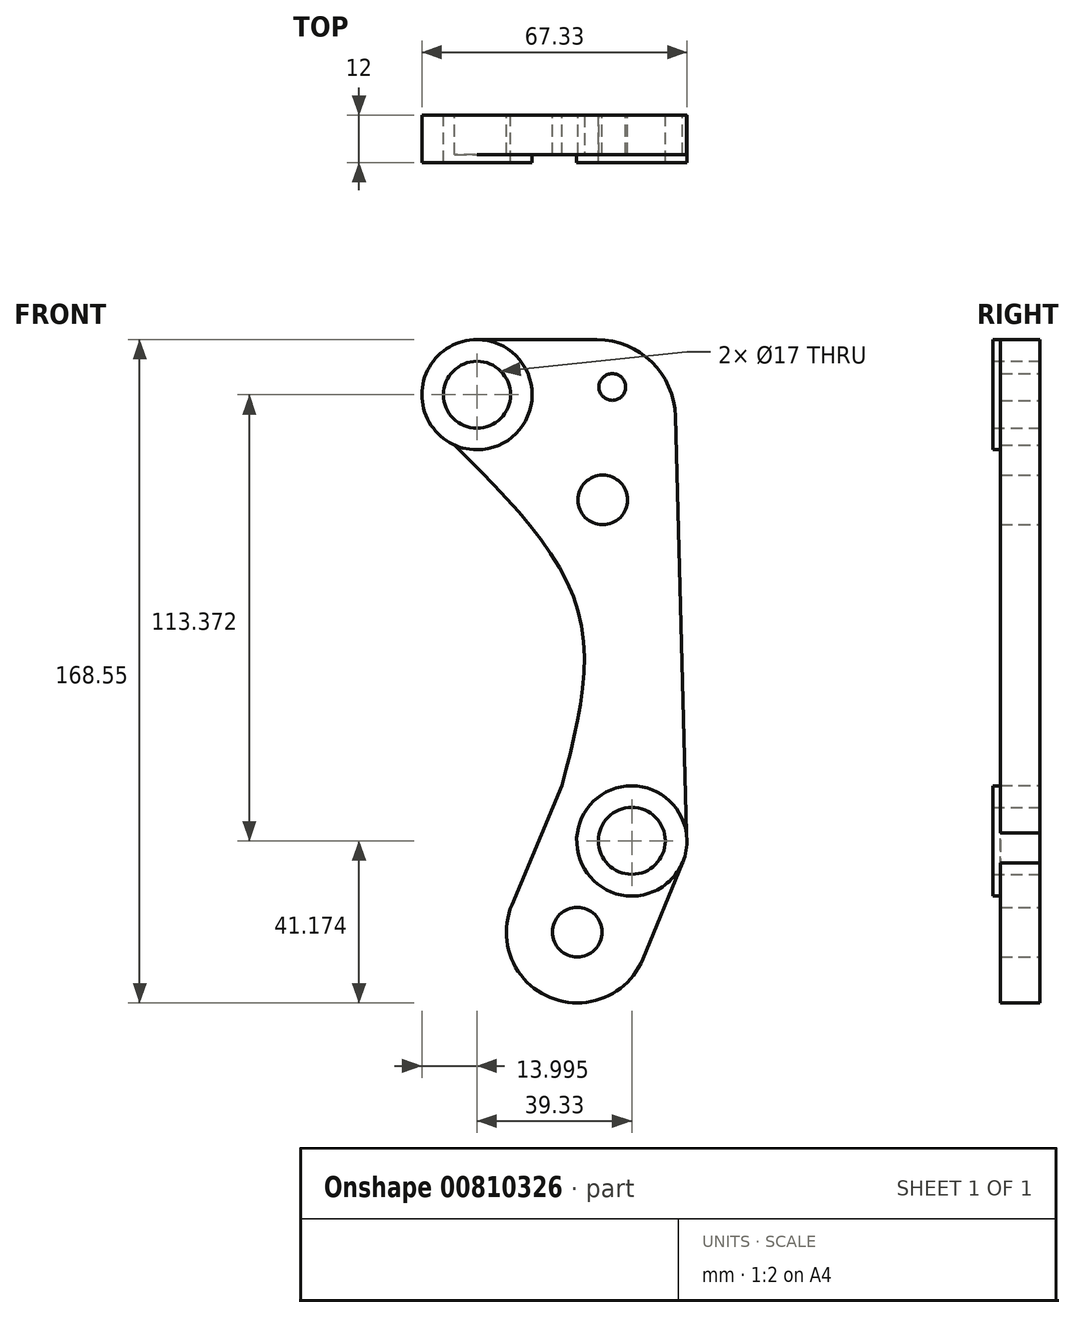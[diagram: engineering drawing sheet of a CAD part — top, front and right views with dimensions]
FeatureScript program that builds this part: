
annotation { "Feature Type Name" : "Feature", "Feature Type Description" : "" }
export const myFeature = defineFeature(function(context is Context, id is Id, definition is map)
    precondition{}
    {
        {
            var Q0;
            Q0=qCreatedBy(makeId("Front.planeOp"),FACE);
            var sketch = newSketch(context, id + "F0", { "sketchPlane" : qUnion([Q0])});
            skCircle(sketch, "E0", {"center": v(31.19, -37.2) * mm, "radius": 6.3 * mm});
            skCircle(sketch, "E1", {"center": v(37.66, 72.6) * mm, "radius": 6.3 * mm});
            skCircle(sketch, "E2", {"center": v(45.05, -14.04) * mm, "radius": 8.5 * mm});
            skCircle(sketch, "E3", {"center": v(45.05, -14.04) * mm, "radius": 14 * mm});
            skArc(sketch, "E4", {"start": v(14.6, -30.24) * mm, "mid": v(24.28, -53.83) * mm, "end": v(47.84, -44.06) * mm});
            skCircle(sketch, "E5", {"center": v(31.19, -37.2) * mm, "radius": 9 * mm});
            skCircle(sketch, "E6", {"center": v(37.66, 72.6) * mm, "radius": 9 * mm});
            skLineSegment(sketch, "E7", {"start": v(57.9, -19.57) * mm, "end": v(47.84, -44.06) * mm});
            skCircle(sketch, "E8", {"center": v(5.72, 99.34) * mm, "radius": 8.5 * mm});
            skCircle(sketch, "E9", {"center": v(5.72, 99.34) * mm, "radius": 14 * mm});
            skArc(sketch, "E10", {"start": v(56.14, 93.81) * mm, "mid": v(50.12, 107.61) * mm, "end": v(36.18, 113.3) * mm});
            skCircle(sketch, "E11", {"center": v(40.1, 101.3) * mm, "radius": 3.4 * mm});
            skLineSegment(sketch, "E12", {"start": v(36.18, 113.3) * mm, "end": v(5.73, 113.34) * mm});
            skLineSegment(sketch, "E13", {"start": v(58.9, -11.97) * mm, "end": v(56.14, 93.81) * mm});
            skLineSegment(sketch, "E14", {"start": v(14.6, -30.24) * mm, "end": v(27.3, 0) * mm});
            skFitSpline(sketch, "E15", {"points": [v(27.3, 0) * mm, v(31.38, 44.5) * mm, v(0, 86.56) * mm], "startDerivative": vector(25.04, 95.56) * mm, "endDerivative": vector(-78.25, 77.8) * mm});
            skSolve(sketch);
        }
        {
            var Q0;
            Q0=makeQuery(id+"F0.imprint","IMPRINT",FACE,{"disambiguationData":[TD([[makeQuery(id+"F0.imprint","IMPRINT",EDGE,{"derivedFrom":sQuery(id+"F0.wireOp",EDGE,"E2")}),-1.0]])]});
            var Q1;
            Q1=makeQuery(id+"F0.imprint","IMPRINT",FACE,{"disambiguationData":[TD([[makeQuery(id+"F0.imprint","IMPRINT",EDGE,{"derivedFrom":sQuery(id+"F0.wireOp",EDGE,"SP4YICm1-ePz9-ccjE-kNvD-3VjDllcA9a2P")}),1.0]])]});
            var Q2;
            Q2=makeQuery(id+"F0.imprint","IMPRINT",FACE,{"disambiguationData":[TD([[makeQuery(id+"F0.imprint","IMPRINT",EDGE,{"derivedFrom":sQuery(id+"F0.wireOp",EDGE,"E1")}),-1.0]])]});
            var Q3;
            {var subQ0=sQuery(id+"F0.wireOp",EDGE,"E7");Q3=makeQuery(id+"F0.imprint","IMPRINT",FACE,{"disambiguationData":[TD([[makeQuery(id+"F0.imprint","IMPRINT",EDGE,{"derivedFrom":subQ0}),-1.0]])]});}
            var Q4;
            Q4=makeQuery(id+"F0.imprint","IMPRINT",FACE,{"disambiguationData":[TD([[makeQuery(id+"F0.imprint","IMPRINT",EDGE,{"derivedFrom":sQuery(id+"F0.wireOp",EDGE,"E8")}),-1.0]])]});
            var Q5;
            Q5=makeQuery(id+"F0.imprint","IMPRINT",FACE,{"disambiguationData":[TD([[makeQuery(id+"F0.imprint","IMPRINT",EDGE,{"derivedFrom":sQuery(id+"F0.wireOp",EDGE,"E5")}),-1.0]])]});
            var Q6;
            {var subQ2=sQuery(id+"F0.wireOp",EDGE,"E3");var subQ4=sQuery(id+"F0.wireOp",EDGE,"EtesAAMI-uVo2-qHGR-uLT1-KKP0nME1nuCn");var subQ5=makeQuery(id+"F0.imprint","INTERSECT",VERTEX,{"disambiguationData":[OD(0.0)],"derivedFrom":[subQ4,subQ2]});Q6=makeQuery(id+"F0.imprint","IMPRINT",FACE,{"disambiguationData":[TD([[makeQuery(id+"F0.imprint","IMPRINT",EDGE,{"disambiguationData":[TD([[subQ5,-1.0]])],"derivedFrom":subQ4}),-1.0]])]});}
            var Q7;
            Q7=makeQuery(id+"F0.imprint","IMPRINT",FACE,{"disambiguationData":[TD([[makeQuery(id+"F0.imprint","IMPRINT",EDGE,{"derivedFrom":sQuery(id+"F0.wireOp",EDGE,"SP4YICm1-ePz9-ccjE-kNvD-3VjDllcA9a2P")}),-1.0]])]});
            var Q8;
            Q8=makeQuery(id+"F0.imprint","IMPRINT",FACE,{"disambiguationData":[TD([[makeQuery(id+"F0.imprint","IMPRINT",EDGE,{"derivedFrom":sQuery(id+"F0.wireOp",EDGE,"E0")}),1.0]])]});
            var Q9;
            Q9=makeQuery(id+"F0.imprint","IMPRINT",FACE,{"disambiguationData":[TD([[makeQuery(id+"F0.imprint","IMPRINT",EDGE,{"derivedFrom":sQuery(id+"F0.wireOp",EDGE,"E1")}),1.0]])]});
            var Q10;
            Q10=makeQuery(id+"F0.imprint","IMPRINT",FACE,{"disambiguationData":[TD([[makeQuery(id+"F0.imprint","IMPRINT",EDGE,{"derivedFrom":sQuery(id+"F0.wireOp",EDGE,"E2")}),1.0]])]});
            var Q11;
            Q11=makeQuery(id+"F0.imprint","IMPRINT",FACE,{"disambiguationData":[TD([[makeQuery(id+"F0.imprint","IMPRINT",EDGE,{"derivedFrom":sQuery(id+"F0.wireOp",EDGE,"E8")}),1.0]])]});
            var Q12;
            Q12=makeQuery(id+"F0.imprint","IMPRINT",FACE,{"disambiguationData":[TD([[makeQuery(id+"F0.imprint","IMPRINT",EDGE,{"derivedFrom":sQuery(id+"F0.wireOp",EDGE,"E11")}),1.0]])]});
            var Q13;
            Q13=makeQuery(id+"F0.imprint","IMPRINT",FACE,{"disambiguationData":[TD([[makeQuery(id+"F0.imprint","IMPRINT",EDGE,{"derivedFrom":sQuery(id+"F0.wireOp",EDGE,"E0")}),-1.0]])]});
            var Q14;
            {var subQ0=sQuery(id+"F0.wireOp",EDGE,"E3");var subQ1=sQuery(id+"F0.wireOp",EDGE,"EtesAAMI-uVo2-qHGR-uLT1-KKP0nME1nuCn");var subQ2=makeQuery(id+"F0.imprint","INTERSECT",VERTEX,{"disambiguationData":[OD(0.0)],"derivedFrom":[subQ1,subQ0]});Q14=makeQuery(id+"F0.imprint","IMPRINT",FACE,{"disambiguationData":[TD([[makeQuery(id+"F0.imprint","IMPRINT",EDGE,{"disambiguationData":[TD([[subQ2,1.0]])],"derivedFrom":subQ1}),-1.0]])]});}
            var Q15;
            {var subQ0=sQuery(id+"F0.wireOp",EDGE,"E3");var subQ1=sQuery(id+"F0.wireOp",EDGE,"EtesAAMI-uVo2-qHGR-uLT1-KKP0nME1nuCn");var subQ2=makeQuery(id+"F0.imprint","INTERSECT",VERTEX,{"disambiguationData":[OD(0.0)],"derivedFrom":[subQ1,subQ0]});Q15=makeQuery(id+"F0.imprint","IMPRINT",FACE,{"disambiguationData":[TD([[makeQuery(id+"F0.imprint","IMPRINT",EDGE,{"disambiguationData":[TD([[subQ2,1.0]])],"derivedFrom":subQ1}),1.0]])]});}
            var Q16;
            {var subQ0=sQuery(id+"F0.wireOp",EDGE,"E12");var subQ1=sQuery(id+"F0.wireOp",EDGE,"E10");var subQ2=makeQuery(id+"F0.imprint","INTERSECT",VERTEX,{"disambiguationData":[OD(0.0)],"derivedFrom":[subQ1,subQ0]});Q16=makeQuery(id+"F0.imprint","IMPRINT",FACE,{"disambiguationData":[TD([[makeQuery(id+"F0.imprint","IMPRINT",EDGE,{"disambiguationData":[TD([[subQ2,-1.0]])],"derivedFrom":subQ1}),1.0]])]});}
            var Q17;
            Q17=sQuery(id+"F0.wireOp",EDGE,"E15");
            var Q18;
            Q18=sQuery(id+"F0.wireOp",EDGE,"E9");
            var Q19;
            Q19=sQuery(id+"F0.wireOp",EDGE,"E12");
            var Q20;
            Q20=sQuery(id+"F0.wireOp",EDGE,"E10");
            var Q21;
            Q21=sQuery(id+"F0.wireOp",EDGE,"E13");
            var Q22;
            Q22=sQuery(id+"F0.wireOp",EDGE,"E7");
            var Q23;
            Q23=sQuery(id+"F0.wireOp",EDGE,"E14");
            var Q24;
            Q24=sQuery(id+"F0.wireOp",EDGE,"E4");
            var Q25;
            Q25=sQuery(id+"F0.wireOp",EDGE,"E3");
            extrude(context, id + "F1", {"entities" : qUnion([Q0, Q1, Q2, Q3, Q4, Q5, Q6, Q7, Q8, Q9, Q10, Q11, Q12, Q13, Q14, Q15, Q16]), "surfaceEntities" : qUnion([Q17, Q18, Q19, Q20, Q21, Q22, Q23, Q24, Q25]), "depth" : 10 * mm, "offsetDistance" : 25 * mm});
        }
        {
            var Q0;
            Q0=makeQuery(id+"F0.imprint","IMPRINT",FACE,{"disambiguationData":[TD([[makeQuery(id+"F0.imprint","IMPRINT",EDGE,{"derivedFrom":sQuery(id+"F0.wireOp",EDGE,"E8")}),-1.0]])]});
            var Q1;
            Q1=sQuery(id+"F0.wireOp",EDGE,"E9");
            extrude(context, id + "F2", {"entities" : qUnion([Q0]), "operationType" : NewBodyOperationType.ADD, "surfaceEntities" : qUnion([Q1]), "depth" : 12 * mm, "offsetDistance" : 25 * mm});
        }
        {
            var Q0;
            Q0=makeQuery(id+"F2.boolean.opBoolean","SPLIT",FACE,{"disambiguationData":[TD([makeQuery(id+"F2.opExtrude","SWEPT_FACE",FACE,{"disambiguationData":[OSD([sQuery(id+"F0.wireOp",EDGE,"E8")])]})])],"derivedFrom":makeQuery(id+"F1.opExtrude","CAP_FACE",FACE,{"disambiguationData":[OSD([sQuery(id+"F0.wireOp",EDGE,"E3"),sQuery(id+"F0.wireOp",EDGE,"E4"),sQuery(id+"F0.wireOp",EDGE,"E7"),sQuery(id+"F0.wireOp",EDGE,"E9"),sQuery(id+"F0.wireOp",EDGE,"E10"),sQuery(id+"F0.wireOp",EDGE,"E12"),sQuery(id+"F0.wireOp",EDGE,"E13"),sQuery(id+"F0.wireOp",EDGE,"E14"),sQuery(id+"F0.wireOp",EDGE,"E15")])],"isStart":false})});
            extrude(context, id + "F3", {"entities" : qUnion([Q0]), "operationType" : NewBodyOperationType.REMOVE, "oppositeDirection" : true, "depth" : 10 * mm, "offsetDistance" : 25 * mm});
        }
        {
            var Q0;
            Q0=makeQuery(id+"F0.imprint","IMPRINT",FACE,{"disambiguationData":[TD([[makeQuery(id+"F0.imprint","IMPRINT",EDGE,{"derivedFrom":sQuery(id+"F0.wireOp",EDGE,"E11")}),1.0]])]});
            extrude(context, id + "F4", {"entities" : qUnion([Q0]), "operationType" : NewBodyOperationType.REMOVE, "oppositeDirection" : true, "depth" : -10 * mm, "offsetDistance" : 25 * mm});
        }
        {
            var Q0;
            Q0=makeQuery(id+"F0.imprint","IMPRINT",FACE,{"disambiguationData":[TD([[makeQuery(id+"F0.imprint","IMPRINT",EDGE,{"derivedFrom":sQuery(id+"F0.wireOp",EDGE,"E1")}),1.0]])]});
            var Q1;
            Q1=sQuery(id+"F0.wireOp",EDGE,"E1");
            extrude(context, id + "F5", {"entities" : qUnion([Q0]), "operationType" : NewBodyOperationType.REMOVE, "surfaceEntities" : qUnion([Q1]), "oppositeDirection" : true, "depth" : -10 * mm, "offsetDistance" : 25 * mm});
        }
        {
            var Q0;
            Q0=makeQuery(id+"F0.imprint","IMPRINT",FACE,{"disambiguationData":[TD([[makeQuery(id+"F0.imprint","IMPRINT",EDGE,{"derivedFrom":sQuery(id+"F0.wireOp",EDGE,"E2")}),-1.0]])]});
            extrude(context, id + "F6", {"entities" : qUnion([Q0]), "operationType" : NewBodyOperationType.ADD, "depth" : 12 * mm, "offsetDistance" : 25 * mm});
        }
        {
            var Q0;
            {var subQ0=sQuery(id+"F0.wireOp",EDGE,"E7");var subQ1=sQuery(id+"F0.wireOp",EDGE,"E4");var subQ2=sQuery(id+"F0.wireOp",EDGE,"E9");var subQ3=sQuery(id+"F0.wireOp",EDGE,"E3");var subQ4=sQuery(id+"F0.wireOp",EDGE,"E10");var subQ5=sQuery(id+"F0.wireOp",EDGE,"E12");var subQ6=sQuery(id+"F0.wireOp",EDGE,"E13");var subQ7=sQuery(id+"F0.wireOp",EDGE,"E14");var subQ8=sQuery(id+"F0.wireOp",EDGE,"E15");Q0=makeQuery(id+"F6.boolean.opBoolean","SPLIT",FACE,{"disambiguationData":[TD([makeQuery(id+"F6.opExtrude","SWEPT_FACE",FACE,{"disambiguationData":[OSD([sQuery(id+"F0.wireOp",EDGE,"E2")])]})])],"derivedFrom":makeQuery(id+"F2.boolean.opBoolean","SPLIT",FACE,{"disambiguationData":[TD([makeQuery(id+"F1.opExtrude","SWEPT_FACE",FACE,{"disambiguationData":[OSD([subQ3])]})])],"derivedFrom":makeQuery(id+"F1.opExtrude","CAP_FACE",FACE,{"disambiguationData":[OSD([subQ3,subQ1,subQ0,subQ2,subQ4,subQ5,subQ6,subQ7,subQ8])],"isStart":false})})});}
            extrude(context, id + "F7", {"entities" : qUnion([Q0]), "operationType" : NewBodyOperationType.REMOVE, "oppositeDirection" : true, "depth" : 10 * mm, "offsetDistance" : 25 * mm});
        }
        {
            var Q0;
            Q0=makeQuery(id+"F0.imprint","IMPRINT",FACE,{"disambiguationData":[TD([[makeQuery(id+"F0.imprint","IMPRINT",EDGE,{"derivedFrom":sQuery(id+"F0.wireOp",EDGE,"E0")}),1.0]])]});
            extrude(context, id + "F8", {"entities" : qUnion([Q0]), "operationType" : NewBodyOperationType.REMOVE, "oppositeDirection" : true, "depth" : -10 * mm, "offsetDistance" : 25 * mm});
        }
    });
